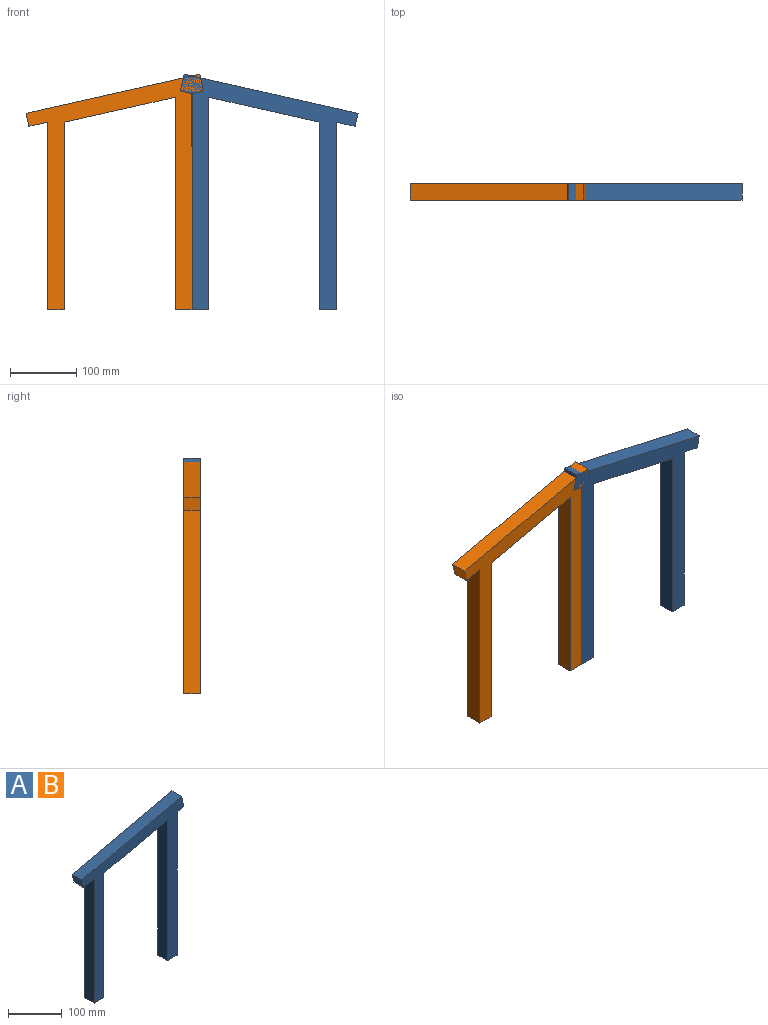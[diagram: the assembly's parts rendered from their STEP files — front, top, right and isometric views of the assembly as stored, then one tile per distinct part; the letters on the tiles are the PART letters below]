
ASSEMBLY  parts=2 mates=1
PART A: 14 faces, bbox 268.1x25.4x355.7 mm
  f0: plane 283.29x25.4mm, normal (-1,0,0), area 7195.5mm2, adj f1,f11,f12,f13
  f1: plane 25.4x25.4mm, normal (0,0,-1), area 645.2mm2, adj f0,f2,f12,f13
  f2: plane 283.29x25.4mm, normal (1,0,0), area 7195.5mm2, adj f1,f3,f12,f13
  f3: plane 167.47x37.59mm, normal (0.22,0,-0.98), area 4359.5mm2, adj f2,f4,f12,f13
  f4: plane 320.88x25.4mm, normal (-1,0,0), area 8150.4mm2, adj f3,f5,f12,f13
  f5: plane 25.4x25.4mm, normal (0,0,-1), area 645.2mm2, adj f4,f6,f12,f13
  f6: plane 326.58x25.4mm, normal (1,0,0), area 8295.2mm2, adj f5,f7,f12,f13
  f7: plane 25.4x17.42mm, normal (0.22,0,-0.98), area 453.6mm2, adj f6,f8,f12,f13
  f8: plane 25.4x25.18mm, normal (0.98,0,0.22), area 655.4mm2, adj f7,f9,f12,f13
  f9: plane 262.47x58.92mm, normal (-0.22,0,0.98), area 6832.5mm2, adj f8,f10,f12,f13
  f10: plane 25.4x19.75mm, normal (-0.98,0,-0.22), area 514.1mm2, adj f9,f11,f12,f13
  f11: plane 27.99x25.4mm, normal (0.22,0,-0.98), area 728.8mm2, adj f0,f10,f12,f13
  f12: plane 355.67x268.12mm, normal (0,1,0), area 22130.5mm2, adj f0,f1,f2,f3,f4,f5,f6,f7
  f13: plane 355.67x268.12mm, normal (0,-1,0), area 22130.5mm2, adj f0,f1,f2,f3,f4,f5,f6,f7
PART B: same geometry as A
PLACE A rot(axis=(0,0,1),180deg) t=(-100.33,-79.09,12.24)mm
PLACE B t=(-151.13,-79.09,12.24)mm
MATE parallel A.f6 <-> B.f6  axis (-1,0,0) through (-125.73,-79.09,-37.13)mm
